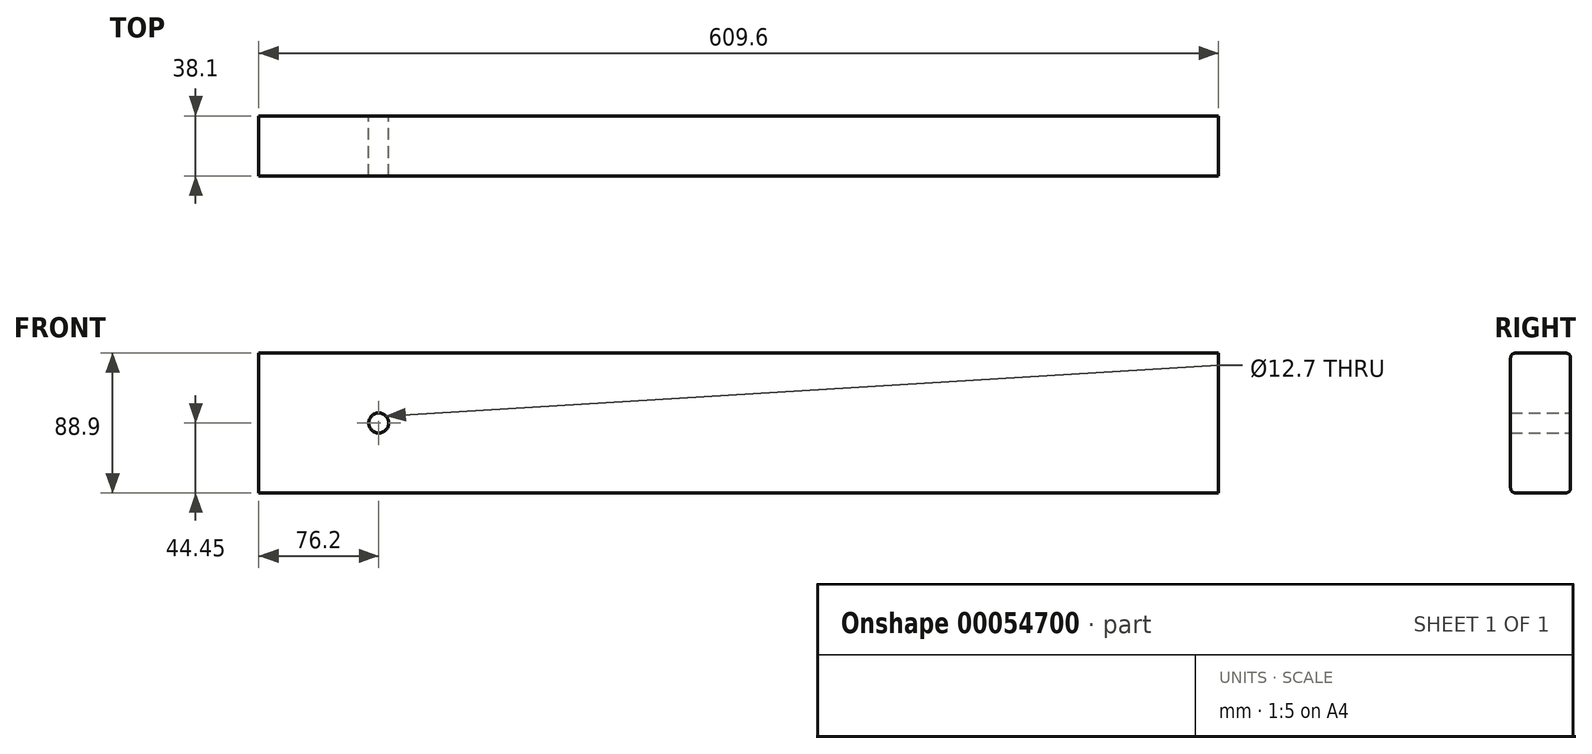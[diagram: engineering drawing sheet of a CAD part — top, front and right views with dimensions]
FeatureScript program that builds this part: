
annotation { "Feature Type Name" : "Feature", "Feature Type Description" : "" }
export const myFeature = defineFeature(function(context is Context, id is Id, definition is map)
    precondition{}
    {
        {
            var Q0;
            Q0=qCreatedBy(makeId("Front.planeOp"),FACE);
            var sketch = newSketch(context, id + "F0", { "sketchPlane" : qUnion([Q0])});
            skLineSegment(sketch, "E0.rect.bottom", {"start": v(-304.8, -44.45) * mm, "end": v(304.8, -44.45) * mm});
            skLineSegment(sketch, "E0.rect.top", {"start": v(-304.8, 44.45) * mm, "end": v(304.8, 44.45) * mm});
            skLineSegment(sketch, "E0.rect.left", {"start": v(-304.8, -44.45) * mm, "end": v(-304.8, 44.45) * mm});
            skLineSegment(sketch, "E0.rect.right", {"start": v(304.8, -44.45) * mm, "end": v(304.8, 44.45) * mm});
            skPoint(sketch, "E0.rect.middle", {"position": v(0, 0) * mm});
            skCircle(sketch, "E1", {"center": v(-228.6, 0) * mm, "radius": 6.35 * mm});
            skSolve(sketch);
        }
        {
            var Q0;
            Q0=makeQuery(id+"F0.imprint","IMPRINT",FACE,{"disambiguationData":[TD([[makeQuery(id+"F0.imprint","IMPRINT",EDGE,{"derivedFrom":sQuery(id+"F0.wireOp",EDGE,"E0.rect.bottom")}),1.0]])]});
            extrude(context, id + "F1", {"entities" : qUnion([Q0]), "depth" : 38.1 * mm});
        }
        {
            var Q0;
            Q0=makeQuery(id+"F1.opExtrude","CAP_EDGE",EDGE,{"disambiguationData":[OSD([sQuery(id+"F0.wireOp",EDGE,"E0.rect.top")])],"isStart":false});
            var Q1;
            Q1=makeQuery(id+"F1.opExtrude","CAP_EDGE",EDGE,{"disambiguationData":[OSD([sQuery(id+"F0.wireOp",EDGE,"E0.rect.bottom")])],"isStart":false});
            var Q2;
            Q2=makeQuery(id+"F1.opExtrude","CAP_EDGE",EDGE,{"disambiguationData":[OSD([sQuery(id+"F0.wireOp",EDGE,"E0.rect.top")])],"isStart":true});
            var Q3;
            Q3=makeQuery(id+"F1.opExtrude","CAP_EDGE",EDGE,{"disambiguationData":[OSD([sQuery(id+"F0.wireOp",EDGE,"E0.rect.bottom")])],"isStart":true});
            fillet(context, id + "F2", {"entities" : qUnion([Q0, Q1, Q2, Q3]), "radius" : 3.17 * mm, "tangentPropagation" : true, "allowEdgeOverflow" : false});
        }
    });
